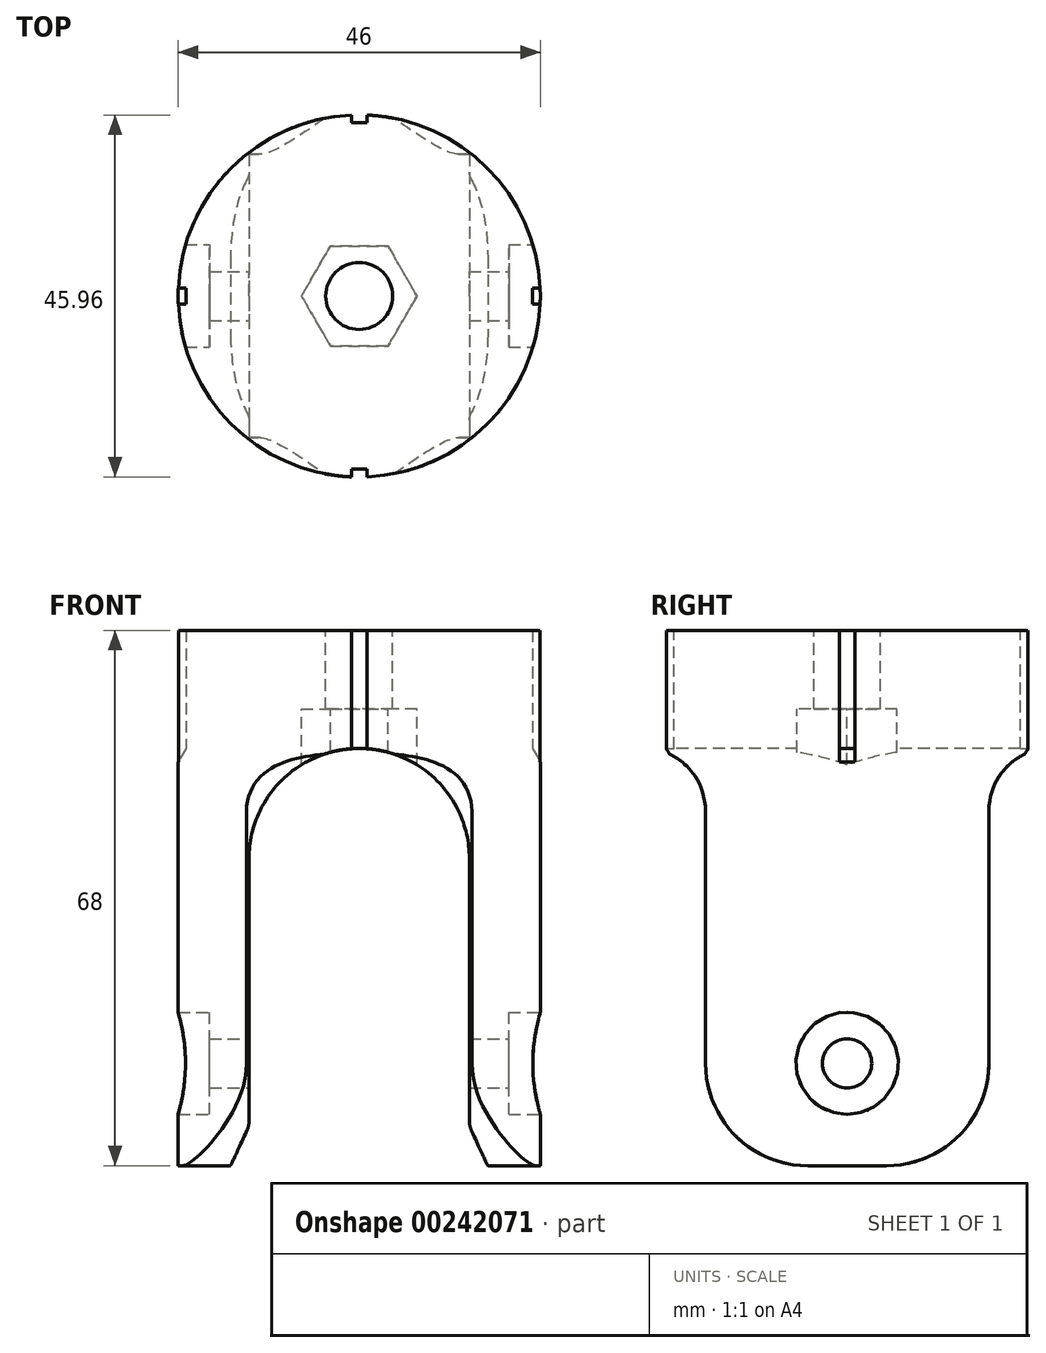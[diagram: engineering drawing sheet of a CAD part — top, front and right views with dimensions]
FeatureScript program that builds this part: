
annotation { "Feature Type Name" : "Feature", "Feature Type Description" : "" }
export const myFeature = defineFeature(function(context is Context, id is Id, definition is map)
    precondition{}
    {
        {
            var Q0;
            Q0=qCreatedBy(makeId("Top.planeOp"),FACE);
            var sketch = newSketch(context, id + "F0", { "sketchPlane" : qUnion([Q0])});
            skCircle(sketch, "E0", {"center": v(0, 0) * mm, "radius": 23 * mm});
            skSolve(sketch);
        }
        {
            var Q0;
            Q0=qSketchRegion(id+"F0",true);
            extrude(context, id + "F1", {"entities" : qUnion([Q0]), "oppositeDirection" : true, "depth" : 68 * mm});
        }
        {
            var Q0;
            Q0=qCreatedBy(makeId("Right.planeOp"),FACE);
            var sketch = newSketch(context, id + "F2", { "sketchPlane" : qUnion([Q0])});
            skCircle(sketch, "E1", {"center": v(0, -55) * mm, "radius": 40 * mm, "construction": true});
            skLineSegment(sketch, "E2", {"start": v(-28, -15) * mm, "end": v(-25, -15) * mm});
            skLineSegment(sketch, "E3", {"start": v(-18, -22.94) * mm, "end": v(-18, -55) * mm});
            skLineSegment(sketch, "E4", {"start": v(-28, -15) * mm, "end": v(-28, -73) * mm});
            skLineSegment(sketch, "E5", {"start": v(-28, -73) * mm, "end": v(0, -73) * mm});
            skLineSegment(sketch, "E6", {"start": v(0, -68) * mm, "end": v(-5, -68) * mm});
            skArc(sketch, "E7", {"start": v(-18, -55) * mm, "mid": v(-14.2, -64.2) * mm, "end": v(-5, -68) * mm});
            skLineSegment(sketch, "E8", {"start": v(0, 0) * mm, "end": v(0, -95) * mm, "construction": true});
            skArc(sketch, "E9", {"start": v(-18, -22.94) * mm, "mid": v(-20, -17.65) * mm, "end": v(-25, -15) * mm});
            skLineSegment(sketch, "E10.MirrorCS", {"start": v(28, -15) * mm, "end": v(25, -15) * mm});
            skArc(sketch, "E11.MirrorCS", {"start": v(18, -22.94) * mm, "mid": v(20, -17.65) * mm, "end": v(25, -15) * mm});
            skArc(sketch, "E12.MirrorCS", {"start": v(18, -55) * mm, "mid": v(14.2, -64.2) * mm, "end": v(5, -68) * mm});
            skLineSegment(sketch, "E13.MirrorCS", {"start": v(0, -68) * mm, "end": v(5, -68) * mm});
            skLineSegment(sketch, "E14.MirrorCS", {"start": v(18, -22.94) * mm, "end": v(18, -55) * mm});
            skLineSegment(sketch, "E15.MirrorCS", {"start": v(28, -73) * mm, "end": v(0, -73) * mm});
            skLineSegment(sketch, "E16.MirrorCS", {"start": v(28, -15) * mm, "end": v(28, -73) * mm});
            skSolve(sketch);
        }
        {
            var Q0;
            Q0=qSketchRegion(id+"F2",true);
            extrude(context, id + "F3", {"entities" : qUnion([Q0]), "operationType" : NewBodyOperationType.REMOVE, "endBound" : BoundingType.THROUGH_ALL, "oppositeDirection" : true, "depth" : 25 * mm, "hasSecondDirection" : true, "secondDirectionBound" : SecondDirectionBoundingType.THROUGH_ALL, "secondDirectionOppositeDirection" : false, "secondDirectionDepth" : 25 * mm});
        }
        {
            var Q0;
            Q0=qCreatedBy(makeId("Front.planeOp"),FACE);
            var sketch = newSketch(context, id + "F4", { "sketchPlane" : qUnion([Q0])});
            skArc(sketch, "E17", {"start": v(14, -29) * mm, "mid": v(0, -15) * mm, "end": v(-14, -29) * mm});
            skLineSegment(sketch, "E18", {"start": v(-14, -29) * mm, "end": v(-14, -62.33) * mm});
            skLineSegment(sketch, "E19", {"start": v(14, -29) * mm, "end": v(14, -62.33) * mm});
            skLineSegment(sketch, "E20", {"start": v(16.33, -68) * mm, "end": v(-16.33, -68) * mm});
            skLineSegment(sketch, "E21", {"start": v(-14.28, -63.6) * mm, "end": v(-16.33, -68) * mm});
            skLineSegment(sketch, "E22", {"start": v(14.28, -63.6) * mm, "end": v(16.33, -68) * mm});
            skLineSegment(sketch, "E23", {"start": v(-14, -63) * mm, "end": v(14, -63) * mm, "construction": true});
            skPoint(sketch, "E24.visualSharp", {"position": v(-14, -63) * mm});
            skArc(sketch, "E24.filletArc", {"start": v(-14.28, -63.6) * mm, "mid": v(-14.07, -62.98) * mm, "end": v(-14, -62.33) * mm});
            skPoint(sketch, "E25.visualSharp", {"position": v(14, -63) * mm});
            skArc(sketch, "E25.filletArc", {"start": v(14, -62.33) * mm, "mid": v(14.07, -62.98) * mm, "end": v(14.28, -63.6) * mm});
            skSolve(sketch);
        }
        {
            var Q0;
            Q0=qSketchRegion(id+"F4",true);
            extrude(context, id + "F5", {"entities" : qUnion([Q0]), "operationType" : NewBodyOperationType.REMOVE, "endBound" : BoundingType.THROUGH_ALL, "oppositeDirection" : true, "depth" : 25 * mm, "hasSecondDirection" : true, "secondDirectionBound" : SecondDirectionBoundingType.THROUGH_ALL, "secondDirectionOppositeDirection" : false, "secondDirectionDepth" : 25 * mm});
        }
        {
            var Q0;
            Q0=qCreatedBy(makeId("Front.planeOp"),FACE);
            var sketch = newSketch(context, id + "F6", { "sketchPlane" : qUnion([Q0])});
            skLineSegment(sketch, "E26", {"start": v(-30.91, -55) * mm, "end": v(31.05, -55) * mm, "construction": true});
            skLineSegment(sketch, "E27", {"start": v(-26, -48.5) * mm, "end": v(-19, -48.5) * mm});
            skLineSegment(sketch, "E28", {"start": v(-19, -48.5) * mm, "end": v(-19, -51.88) * mm});
            skLineSegment(sketch, "E29", {"start": v(-19, -51.88) * mm, "end": v(0, -51.88) * mm});
            skLineSegment(sketch, "E30", {"start": v(-26, -48.5) * mm, "end": v(-26, -55) * mm});
            skLineSegment(sketch, "E31", {"start": v(-26, -55) * mm, "end": v(0, -55) * mm});
            skLineSegment(sketch, "E32.MirrorCS", {"start": v(26, -48.5) * mm, "end": v(19, -48.5) * mm});
            skLineSegment(sketch, "E33.MirrorCS", {"start": v(19, -48.5) * mm, "end": v(19, -51.88) * mm});
            skLineSegment(sketch, "E34.MirrorCS", {"start": v(19, -51.88) * mm, "end": v(0, -51.88) * mm});
            skLineSegment(sketch, "E35.MirrorCS", {"start": v(26, -48.5) * mm, "end": v(26, -55) * mm});
            skLineSegment(sketch, "E36.MirrorCS", {"start": v(26, -55) * mm, "end": v(0, -55) * mm});
            skSolve(sketch);
        }
        {
            var Q0;
            Q0=qSketchRegion(id+"F6",true);
            var Q1;
            Q1=sQuery(id+"F6.wireOp",EDGE,"E26");
            revolve(context, id + "F7", {"operationType" : NewBodyOperationType.REMOVE, "entities" : qUnion([Q0]), "axis" : qUnion([Q1]), "revolveType" : RevolveType.FULL, "oppositeDirection" : true});
        }
        {
            var Q0;
            Q0=makeQuery(id+"F1.opExtrude","CAP_FACE",FACE,{"disambiguationData":[OSD([sQuery(id+"F0.wireOp",EDGE,"E0")])],"isStart":true});
            var sketch = newSketch(context, id + "F8", { "sketchPlane" : qUnion([Q0])});
            skCircle(sketch, "E37", {"center": v(0, 0) * mm, "radius": 4.25 * mm});
            skSolve(sketch);
        }
        {
            var Q0;
            Q0=qSketchRegion(id+"F8",true);
            extrude(context, id + "F9", {"entities" : qUnion([Q0]), "operationType" : NewBodyOperationType.REMOVE, "oppositeDirection" : true, "depth" : 25 * mm});
        }
        {
            var Q0;
            Q0=qCreatedBy(makeId("Top.planeOp"),FACE);
            cPlane(context, id + "F10", {"entities" : qUnion([Q0]), "cplaneType" : CPlaneType.OFFSET, "offset" : 10 * mm, "oppositeDirection" : true, "width" : 150 * mm, "height" : 150 * mm});
        }
        {
            var Q0;
            Q0=qCreatedBy(id+"F10.planeOp",FACE);
            var sketch = newSketch(context, id + "F11", { "sketchPlane" : qUnion([Q0])});
            skCircle(sketch, "E38.cCircle", {"center": v(0, 0) * mm, "radius": 6.35 * mm, "construction": true});
            skLineSegment(sketch, "E38.0", {"start": v(7.33, 0) * mm, "end": v(3.67, -6.35) * mm});
            skLineSegment(sketch, "E38.1", {"start": v(3.67, -6.35) * mm, "end": v(-3.67, -6.35) * mm});
            skLineSegment(sketch, "E38.2", {"start": v(-3.67, -6.35) * mm, "end": v(-7.33, 0) * mm});
            skLineSegment(sketch, "E38.3", {"start": v(-7.33, 0) * mm, "end": v(-3.67, 6.35) * mm});
            skLineSegment(sketch, "E38.4", {"start": v(-3.67, 6.35) * mm, "end": v(3.67, 6.35) * mm});
            skLineSegment(sketch, "E38.5", {"start": v(3.67, 6.35) * mm, "end": v(7.33, 0) * mm});
            skPoint(sketch, "E38.0.midPoint", {"position": v(5.5, -3.18) * mm});
            skSolve(sketch);
        }
        {
            var Q0;
            Q0=qSketchRegion(id+"F11",true);
            extrude(context, id + "F12", {"entities" : qUnion([Q0]), "operationType" : NewBodyOperationType.REMOVE, "oppositeDirection" : true, "depth" : 10 * mm});
        }
        {
            var Q0;
            Q0=makeQuery(id+"F1.opExtrude","CAP_FACE",FACE,{"disambiguationData":[OSD([sQuery(id+"F0.wireOp",EDGE,"E0")])],"isStart":true});
            var sketch = newSketch(context, id + "F13", { "sketchPlane" : qUnion([Q0])});
            skLineSegment(sketch, "E39.bottom", {"start": v(-1, 22) * mm, "end": v(1, 22) * mm});
            skLineSegment(sketch, "E39.top", {"start": v(-1, 24) * mm, "end": v(1, 24) * mm});
            skLineSegment(sketch, "E39.left", {"start": v(-1, 22) * mm, "end": v(-1, 24) * mm});
            skLineSegment(sketch, "E39.right", {"start": v(1, 22) * mm, "end": v(1, 24) * mm});
            skLineSegment(sketch, "E40.bottom", {"start": v(-1, -24) * mm, "end": v(1, -24) * mm});
            skLineSegment(sketch, "E40.top", {"start": v(-1, -22) * mm, "end": v(1, -22) * mm});
            skLineSegment(sketch, "E40.left", {"start": v(-1, -24) * mm, "end": v(-1, -22) * mm});
            skLineSegment(sketch, "E40.right", {"start": v(1, -24) * mm, "end": v(1, -22) * mm});
            skLineSegment(sketch, "E41", {"start": v(0, 18.47) * mm, "end": v(0, -17.11) * mm, "construction": true});
            skPoint(sketch, "E42", {"position": v(0, 22) * mm});
            skPoint(sketch, "E43", {"position": v(0, -22) * mm});
            skSolve(sketch);
        }
        {
            var Q0;
            Q0=qSketchRegion(id+"F13",true);
            extrude(context, id + "F14", {"entities" : qUnion([Q0]), "operationType" : NewBodyOperationType.REMOVE, "oppositeDirection" : true, "depth" : 25 * mm});
        }
        {
            var Q0;
            Q0=qCreatedBy(makeId("Front.planeOp"),FACE);
            var sketch = newSketch(context, id + "F15", { "sketchPlane" : qUnion([Q0])});
            skLineSegment(sketch, "E44", {"start": v(-22, 0) * mm, "end": v(-22, -15) * mm});
            skLineSegment(sketch, "E45", {"start": v(-22, -15) * mm, "end": v(-24, -18.46) * mm});
            skLineSegment(sketch, "E46", {"start": v(-24, -18.46) * mm, "end": v(-25, -18.46) * mm});
            skLineSegment(sketch, "E47", {"start": v(-25, -18.46) * mm, "end": v(-25, 0) * mm});
            skLineSegment(sketch, "E48", {"start": v(-25, 0) * mm, "end": v(-22, 0) * mm});
            skLineSegment(sketch, "E49.MirrorCS", {"start": v(24, -18.46) * mm, "end": v(25, -18.46) * mm});
            skLineSegment(sketch, "E50.MirrorCS", {"start": v(25, 0) * mm, "end": v(22, 0) * mm});
            skLineSegment(sketch, "E51.MirrorCS", {"start": v(22, 0) * mm, "end": v(22, -15) * mm});
            skLineSegment(sketch, "E52.MirrorCS", {"start": v(25, -18.46) * mm, "end": v(25, 0) * mm});
            skLineSegment(sketch, "E53.MirrorCS", {"start": v(22, -15) * mm, "end": v(24, -18.46) * mm});
            skSolve(sketch);
        }
        {
            var Q0;
            Q0=qSketchRegion(id+"F15",true);
            extrude(context, id + "F16", {"entities" : qUnion([Q0]), "operationType" : NewBodyOperationType.REMOVE, "oppositeDirection" : true, "depth" : 1 * mm, "hasSecondDirection" : true, "secondDirectionOppositeDirection" : false, "secondDirectionDepth" : 1 * mm});
        }
    });
